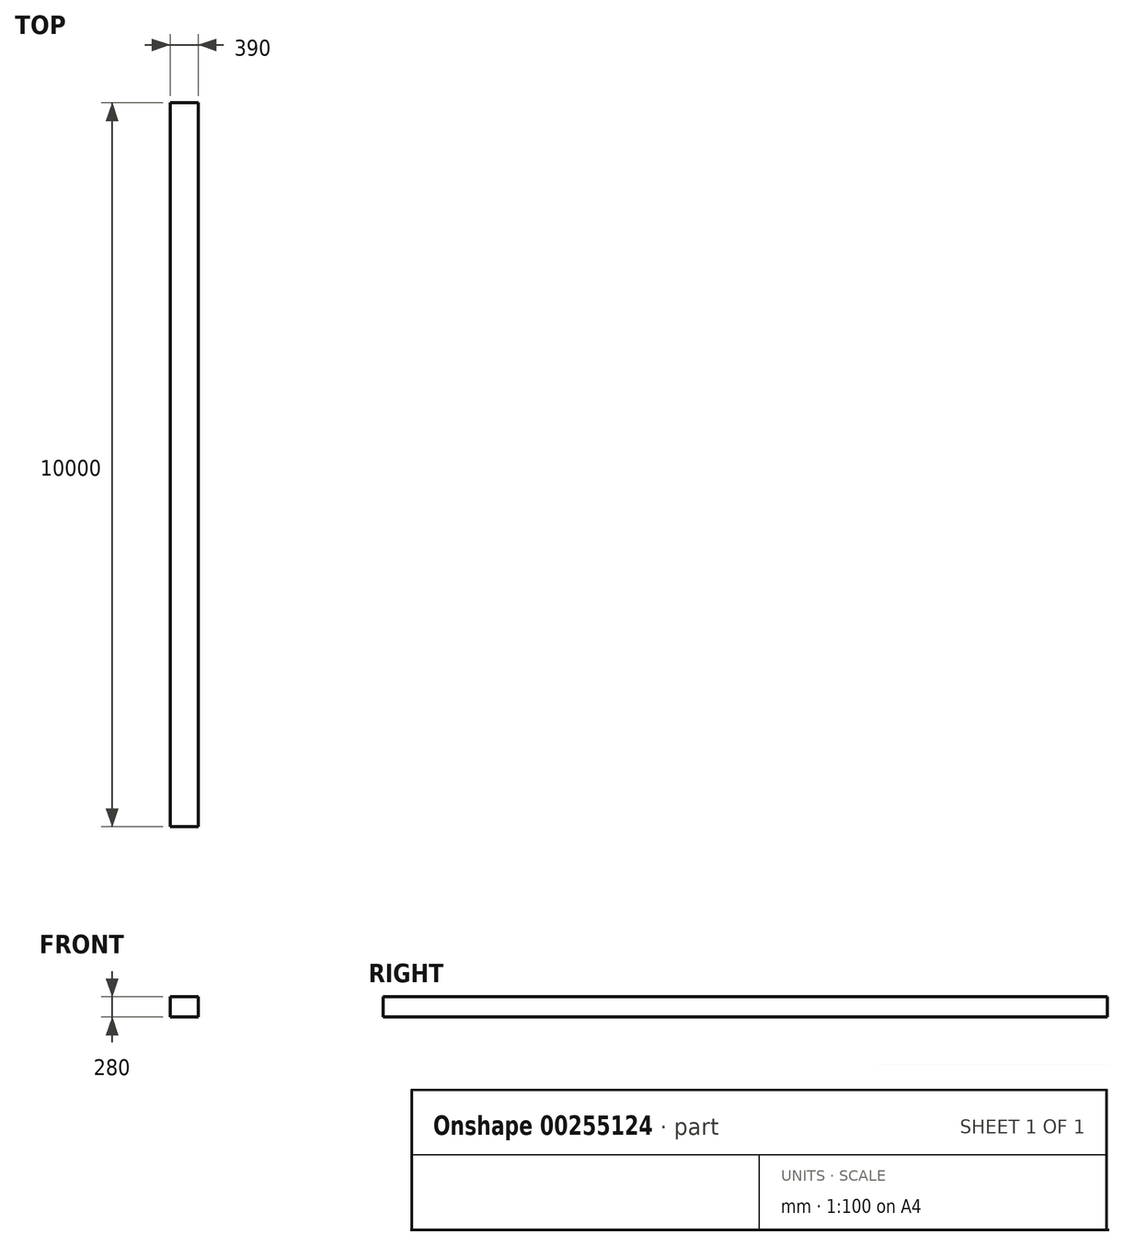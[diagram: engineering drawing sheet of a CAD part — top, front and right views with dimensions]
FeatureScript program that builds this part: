
annotation { "Feature Type Name" : "Feature", "Feature Type Description" : "" }
export const myFeature = defineFeature(function(context is Context, id is Id, definition is map)
    precondition{}
    {
        {
            var Q0;
            Q0=qCreatedBy(makeId("Front.planeOp"),FACE);
            var sketch = newSketch(context, id + "F0", { "sketchPlane" : qUnion([Q0])});
            skLineSegment(sketch, "E0.bottom", {"start": v(195, -140) * mm, "end": v(-195, -140) * mm});
            skLineSegment(sketch, "E0.top", {"start": v(195, 140) * mm, "end": v(-195, 140) * mm});
            skLineSegment(sketch, "E0.left", {"start": v(195, -140) * mm, "end": v(195, 140) * mm});
            skLineSegment(sketch, "E0.right", {"start": v(-195, -140) * mm, "end": v(-195, 140) * mm});
            skPoint(sketch, "E0.middle", {"position": v(0, 0) * mm});
            skSolve(sketch);
        }
        {
            var Q0;
            Q0=makeQuery(id+"F0.imprint","IMPRINT",FACE,{"disambiguationData":[TD([[makeQuery(id+"F0.imprint","IMPRINT",EDGE,{"derivedFrom":sQuery(id+"F0.wireOp",EDGE,"E0.bottom")}),-1.0]])]});
            extrude(context, id + "F1", {"entities" : qUnion([Q0]), "depth" : 10000 * mm});
        }
    });
